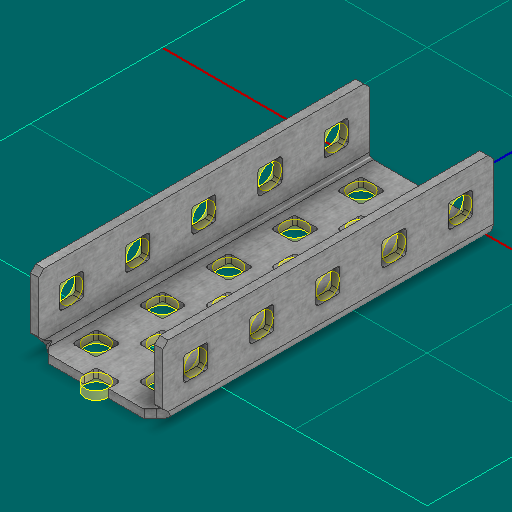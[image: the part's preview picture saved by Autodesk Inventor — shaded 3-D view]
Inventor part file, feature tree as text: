
AUTODESK INVENTOR PART (.ipt)
format: ipt  version: 2025 (Build 290162000, 162)  size: 659,456 bytes
history: native  units: in
note: dims shown in document units (in); Inventor stores cm internally (conversion verified against a paired STEP export)
features: other x56, sketch x5, sheet_metal_op x1
ambient origin geometry x8: Origin, YZ Plane, XZ Plane, XY Plane, X Axis, Y Axis, Z Axis, Center Point
bodies: Solid1 (feature_tree)
feature tree (62):
  other  "Alu C 1x2x1x5.ipt"
  other  "Solid1::Alu C 1x2x1x5.ipt"
  other  "TaggingFeature1"
  sketch  "Sketch1"  dims[d0=0.3937in]
  sketch  "Sketch2"  dims[d1=0.0625in]
  sketch  "Sketch3"
  other  "Flange Pattern Sketch"
  sketch  "Sketch9"
  sheet_metal_op  "Body Pattern Sketch"
  other  "Arc Length"
  sketch  "Sketch14"
  other  "Flange Pattern Plane"
  other  "Srf1"
  other  "Srf2"
  other  "Srf3"
  other  "Srf4"
  other  "Srf5"
  other  "Srf6"
  other  "Srf7"
  other  "Srf8"
  other  "Srf9"
  other  "Srf10"
  other  "Srf11"
  other  "Srf12"
  other  "Srf13"
  other  "Srf14"
  other  "Srf15"
  other  "Srf16"
  other  "Srf17"
  other  "Srf18"
  other  "Srf19"
  other  "Srf20"
  other  "Srf21"
  other  "Srf22"
  other  "Srf23"
  other  "Srf24"
  other  "Srf25"
  other  "Srf1::Derived"
  other  "Srf2::Derived"
  other  "Srf823::Derived"
  other  "Srf824::Derived"
  other  "Srf825::Derived"
  other  "Srf826::Derived"
  other  "Srf827::Derived"
  other  "Srf828::Derived"
  other  "Srf829::Derived"
  other  "Srf922::Derived"
  other  "Srf91::Derived"
  other  "Srf92::Derived"
  other  "Srf856::Derived"
  other  "Srf857::Derived"
  other  "Srf858::Derived"
  other  "Srf859::Derived"
  other  "Srf860::Derived"
  other  "Srf861::Derived"
  other  "Srf862::Derived"
  other  "Srf959::Derived"
  other  "Srf786::Derived"
  other  "Srf889::Derived"
  other  "Srf890::Derived"
  other  "Srf891::Derived"
  other  "Srf892::Derived"
